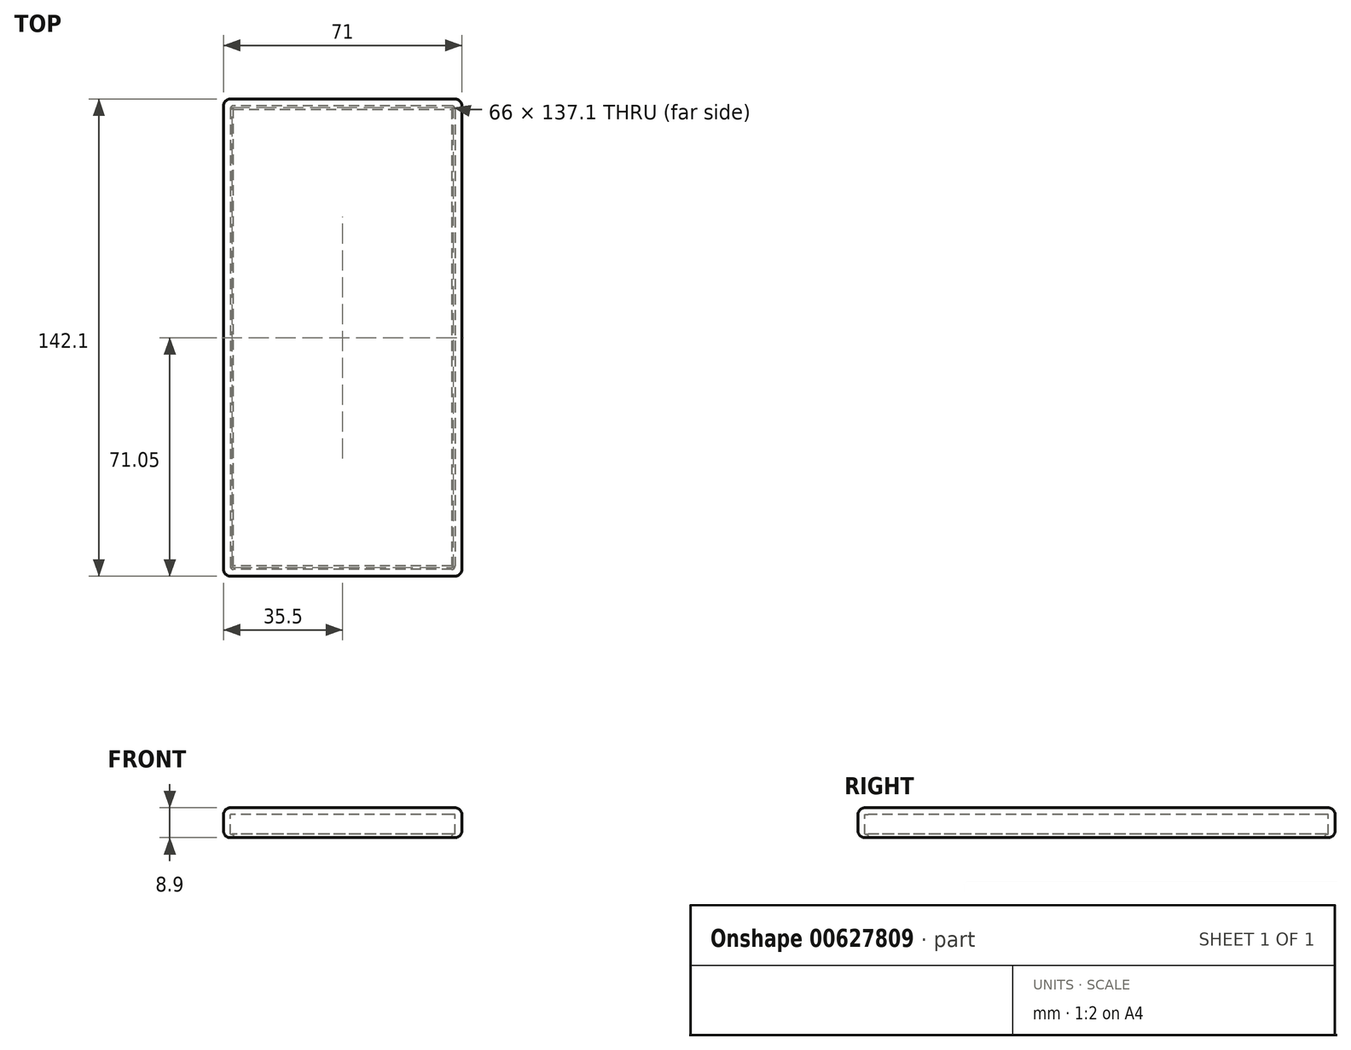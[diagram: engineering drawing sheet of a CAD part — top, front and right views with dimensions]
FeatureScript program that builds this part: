
annotation { "Feature Type Name" : "Feature", "Feature Type Description" : "" }
export const myFeature = defineFeature(function(context is Context, id is Id, definition is map)
    precondition{}
    {
        {
            assignVariable(context, id + "F0", {"name" : "iphone_thickness", "anyValue" : 6.9 * mm});
        }
        {
            assignVariable(context, id + "F1", {"name" : "case_thickness", "anyValue" : 2 * mm});
        }
        {
            var Q0;
            Q0=qCreatedBy(makeId("Top.planeOp"),FACE);
            var sketch = newSketch(context, id + "F2", { "sketchPlane" : qUnion([Q0])});
            skLineSegment(sketch, "E0.bottom", {"start": v(33.5, 69.05) * mm, "end": v(-33.5, 69.05) * mm});
            skLineSegment(sketch, "E0.top", {"start": v(33.5, -69.05) * mm, "end": v(-33.5, -69.05) * mm});
            skLineSegment(sketch, "E0.left", {"start": v(33.5, 69.05) * mm, "end": v(33.5, -69.05) * mm});
            skLineSegment(sketch, "E0.right", {"start": v(-33.5, 69.05) * mm, "end": v(-33.5, -69.05) * mm});
            skPoint(sketch, "E0.middle", {"position": v(0, 0) * mm});
            skLineSegment(sketch, "E1.0", {"start": v(35.5, 71.05) * mm, "end": v(35.5, -71.05) * mm});
            skLineSegment(sketch, "E1.1", {"start": v(35.5, 71.05) * mm, "end": v(-35.5, 71.05) * mm});
            skLineSegment(sketch, "E1.2", {"start": v(-35.5, 71.05) * mm, "end": v(-35.5, -71.05) * mm});
            skLineSegment(sketch, "E1.3", {"start": v(35.5, -71.05) * mm, "end": v(-35.5, -71.05) * mm});
            skSolve(sketch);
        }
        {
            var Q0;
            Q0=makeQuery(id+"F2.imprint","IMPRINT",FACE,{"disambiguationData":[TD([[makeQuery(id+"F2.imprint","IMPRINT",EDGE,{"derivedFrom":sQuery(id+"F2.wireOp",EDGE,"E0.bottom")}),1.0]])]});
            var Q1;
            Q1=makeQuery(id+"F2.imprint","IMPRINT",FACE,{"disambiguationData":[TD([[makeQuery(id+"F2.imprint","IMPRINT",EDGE,{"derivedFrom":sQuery(id+"F2.wireOp",EDGE,"E0.bottom")}),-1.0]])]});
            extrude(context, id + "F3", {"entities" : qUnion([Q0, Q1]), "depth" : getVariable(context, 'case_thickness'), "offsetDistance" : 25 * mm});
        }
        {
            var Q0;
            Q0=makeQuery(id+"F2.imprint","IMPRINT",FACE,{"disambiguationData":[TD([[makeQuery(id+"F2.imprint","IMPRINT",EDGE,{"derivedFrom":sQuery(id+"F2.wireOp",EDGE,"E0.bottom")}),-1.0]])]});
            extrude(context, id + "F4", {"entities" : qUnion([Q0]), "operationType" : NewBodyOperationType.ADD, "oppositeDirection" : true, "depth" : getVariable(context, 'iphone_thickness'), "offsetDistance" : 25 * mm});
        }
        {
            var Q0;
            Q0=makeQuery(id+"F4.opExtrude","CAP_FACE",FACE,{"disambiguationData":[OSD([sQuery(id+"F2.wireOp",EDGE,"E0.bottom"),sQuery(id+"F2.wireOp",EDGE,"E0.top"),sQuery(id+"F2.wireOp",EDGE,"E0.left"),sQuery(id+"F2.wireOp",EDGE,"E0.right"),sQuery(id+"F2.wireOp",EDGE,"E1.0"),sQuery(id+"F2.wireOp",EDGE,"E1.1"),sQuery(id+"F2.wireOp",EDGE,"E1.2"),sQuery(id+"F2.wireOp",EDGE,"E1.3")])],"isStart":false});
            var sketch = newSketch(context, id + "F5", { "sketchPlane" : qUnion([Q0])});
            skLineSegment(sketch, "E2.0", {"start": v(33.5, 69.05) * mm, "end": v(-33.5, 69.05) * mm});
            skLineSegment(sketch, "E2.1", {"start": v(33.5, -69.05) * mm, "end": v(33.5, 69.05) * mm});
            skLineSegment(sketch, "E2.2", {"start": v(-33.5, -69.05) * mm, "end": v(-33.5, 69.05) * mm});
            skLineSegment(sketch, "E2.3", {"start": v(33.5, -69.05) * mm, "end": v(-33.5, -69.05) * mm});
            skLineSegment(sketch, "E3.0", {"start": v(32.5, 68.05) * mm, "end": v(-32.5, 68.05) * mm});
            skLineSegment(sketch, "E3.1", {"start": v(32.5, -68.05) * mm, "end": v(32.5, 68.05) * mm});
            skLineSegment(sketch, "E3.2", {"start": v(32.5, -68.05) * mm, "end": v(-32.5, -68.05) * mm});
            skLineSegment(sketch, "E3.3", {"start": v(-32.5, -68.05) * mm, "end": v(-32.5, 68.05) * mm});
            skLineSegment(sketch, "E4.0", {"start": v(-38.5, 74.05) * mm, "end": v(38.5, 74.05) * mm});
            skLineSegment(sketch, "E4.1", {"start": v(-38.5, -74.05) * mm, "end": v(-38.5, 74.05) * mm});
            skLineSegment(sketch, "E4.2", {"start": v(38.5, -74.05) * mm, "end": v(-38.5, -74.05) * mm});
            skLineSegment(sketch, "E4.3", {"start": v(38.5, 74.05) * mm, "end": v(38.5, -74.05) * mm});
            skSolve(sketch);
        }
        {
            var Q0;
            Q0=makeQuery(id+"F5.imprint","IMPRINT",FACE,{"disambiguationData":[TD([[makeQuery(id+"F5.imprint","IMPRINT",EDGE,{"derivedFrom":sQuery(id+"F5.wireOp",EDGE,"E2.0")}),1.0]])]});
            extrude(context, id + "F6", {"entities" : qUnion([Q0]), "operationType" : NewBodyOperationType.ADD, "oppositeDirection" : true, "depth" : 1 * mm, "offsetDistance" : 25 * mm});
        }
        {
            var Q0;
            Q0=makeQuery(id+"F4.opExtrude","CAP_EDGE",EDGE,{"disambiguationData":[OSD([sQuery(id+"F2.wireOp",EDGE,"E0.left")])],"isStart":true});
            var Q1;
            Q1=makeQuery(id+"F4.opExtrude","CAP_EDGE",EDGE,{"disambiguationData":[OSD([sQuery(id+"F2.wireOp",EDGE,"E1.2")])],"isStart":false});
            var Q2;
            Q2=makeQuery(id+"F3.opExtrude","CAP_EDGE",EDGE,{"disambiguationData":[OSD([sQuery(id+"F2.wireOp",EDGE,"E1.2")])],"isStart":false});
            var Q3;
            Q3=makeQuery(id+"F3.opExtrude","CAP_EDGE",EDGE,{"disambiguationData":[OSD([sQuery(id+"F2.wireOp",EDGE,"E1.1")])],"isStart":false});
            var Q4;
            Q4=makeQuery(id+"F3.opExtrude","CAP_EDGE",EDGE,{"disambiguationData":[OSD([sQuery(id+"F2.wireOp",EDGE,"E1.0")])],"isStart":false});
            var Q5;
            Q5=makeQuery(id+"F3.opExtrude","CAP_EDGE",EDGE,{"disambiguationData":[OSD([sQuery(id+"F2.wireOp",EDGE,"E1.3")])],"isStart":false});
            var Q6;
            {var subQ0=sQuery(id+"F2.wireOp",EDGE,"E1.3");var subQ1=sQuery(id+"F2.wireOp",EDGE,"E1.2");Q6=makeQuery(id+"F4.boolean.opBoolean","MERGE",EDGE,{"derivedFrom":[makeQuery(id+"F3.opExtrude","SWEPT_EDGE",EDGE,{"disambiguationData":[OSD([subQ1,subQ0])]}),makeQuery(id+"F4.opExtrude","SWEPT_EDGE",EDGE,{"disambiguationData":[OSD([subQ1,subQ0])]})]});}
            var Q7;
            {var subQ0=sQuery(id+"F2.wireOp",EDGE,"E1.3");var subQ1=sQuery(id+"F2.wireOp",EDGE,"E1.0");Q7=makeQuery(id+"F4.boolean.opBoolean","MERGE",EDGE,{"derivedFrom":[makeQuery(id+"F3.opExtrude","SWEPT_EDGE",EDGE,{"disambiguationData":[OSD([subQ1,subQ0])]}),makeQuery(id+"F4.opExtrude","SWEPT_EDGE",EDGE,{"disambiguationData":[OSD([subQ1,subQ0])]})]});}
            var Q8;
            {var subQ0=sQuery(id+"F2.wireOp",EDGE,"E1.1");var subQ1=sQuery(id+"F2.wireOp",EDGE,"E1.0");Q8=makeQuery(id+"F4.boolean.opBoolean","MERGE",EDGE,{"derivedFrom":[makeQuery(id+"F3.opExtrude","SWEPT_EDGE",EDGE,{"disambiguationData":[OSD([subQ1,subQ0])]}),makeQuery(id+"F4.opExtrude","SWEPT_EDGE",EDGE,{"disambiguationData":[OSD([subQ1,subQ0])]})]});}
            var Q9;
            {var subQ0=sQuery(id+"F2.wireOp",EDGE,"E1.2");var subQ1=sQuery(id+"F2.wireOp",EDGE,"E1.1");Q9=makeQuery(id+"F4.boolean.opBoolean","MERGE",EDGE,{"derivedFrom":[makeQuery(id+"F3.opExtrude","SWEPT_EDGE",EDGE,{"disambiguationData":[OSD([subQ1,subQ0])]}),makeQuery(id+"F4.opExtrude","SWEPT_EDGE",EDGE,{"disambiguationData":[OSD([subQ1,subQ0])]})]});}
            var Q10;
            Q10=makeQuery(id+"F4.opExtrude","CAP_EDGE",EDGE,{"disambiguationData":[OSD([sQuery(id+"F2.wireOp",EDGE,"E1.1")])],"isStart":false});
            var Q11;
            Q11=makeQuery(id+"F4.opExtrude","CAP_EDGE",EDGE,{"disambiguationData":[OSD([sQuery(id+"F2.wireOp",EDGE,"E1.0")])],"isStart":false});
            var Q12;
            Q12=makeQuery(id+"F4.opExtrude","CAP_EDGE",EDGE,{"disambiguationData":[OSD([sQuery(id+"F2.wireOp",EDGE,"E1.3")])],"isStart":false});
            var Q13;
            Q13=makeQuery(id+"F4.opExtrude","CAP_EDGE",EDGE,{"disambiguationData":[OSD([sQuery(id+"F2.wireOp",EDGE,"E0.top")])],"isStart":true});
            var Q14;
            Q14=makeQuery(id+"F4.opExtrude","CAP_EDGE",EDGE,{"disambiguationData":[OSD([sQuery(id+"F2.wireOp",EDGE,"E0.right")])],"isStart":true});
            var Q15;
            Q15=makeQuery(id+"F4.opExtrude","CAP_EDGE",EDGE,{"disambiguationData":[OSD([sQuery(id+"F2.wireOp",EDGE,"E0.bottom")])],"isStart":true});
            fillet(context, id + "F7", {"entities" : qUnion([Q0, Q1, Q2, Q3, Q4, Q5, Q6, Q7, Q8, Q9, Q10, Q11, Q12, Q13, Q14, Q15]), "radius" : 2 * mm, "tangentPropagation" : true, "allowEdgeOverflow" : false});
        }
        {
            var Q0;
            Q0=makeQuery(id+"F6.opExtrude","CAP_EDGE",EDGE,{"disambiguationData":[OSD([sQuery(id+"F5.wireOp",EDGE,"E3.3")])],"isStart":false});
            var Q1;
            Q1=makeQuery(id+"F6.opExtrude","CAP_EDGE",EDGE,{"disambiguationData":[OSD([sQuery(id+"F5.wireOp",EDGE,"E3.0")])],"isStart":false});
            var Q2;
            Q2=makeQuery(id+"F6.opExtrude","CAP_EDGE",EDGE,{"disambiguationData":[OSD([sQuery(id+"F5.wireOp",EDGE,"E3.1")])],"isStart":false});
            var Q3;
            Q3=makeQuery(id+"F6.opExtrude","CAP_EDGE",EDGE,{"disambiguationData":[OSD([sQuery(id+"F5.wireOp",EDGE,"E3.2")])],"isStart":false});
            var Q4;
            Q4=makeQuery(id+"F6.opExtrude","CAP_EDGE",EDGE,{"disambiguationData":[OSD([sQuery(id+"F5.wireOp",EDGE,"E3.1")])],"isStart":true});
            var Q5;
            Q5=makeQuery(id+"F6.opExtrude","CAP_EDGE",EDGE,{"disambiguationData":[OSD([sQuery(id+"F5.wireOp",EDGE,"E3.2")])],"isStart":true});
            var Q6;
            Q6=makeQuery(id+"F6.opExtrude","CAP_EDGE",EDGE,{"disambiguationData":[OSD([sQuery(id+"F5.wireOp",EDGE,"E3.0")])],"isStart":true});
            var Q7;
            Q7=makeQuery(id+"F7.opFillet","BLEND_EDGE",EDGE,{"blendedFrom":[makeQuery(id+"F4.opExtrude","CAP_EDGE",EDGE,{"disambiguationData":[OSD([sQuery(id+"F2.wireOp",EDGE,"E0.left")])],"isStart":true}),makeQuery(id+"F3.opExtrude","CAP_FACE",FACE,{"disambiguationData":[OSD([sQuery(id+"F2.wireOp",EDGE,"E1.0"),sQuery(id+"F2.wireOp",EDGE,"E1.1"),sQuery(id+"F2.wireOp",EDGE,"E1.2"),sQuery(id+"F2.wireOp",EDGE,"E1.3")])],"isStart":true})],"blendedInto":[makeQuery(id+"F3.opExtrude","CAP_FACE",FACE,{"disambiguationData":[OSD([sQuery(id+"F2.wireOp",EDGE,"E1.0"),sQuery(id+"F2.wireOp",EDGE,"E1.1"),sQuery(id+"F2.wireOp",EDGE,"E1.2"),sQuery(id+"F2.wireOp",EDGE,"E1.3")])],"isStart":true})]});
            var Q8;
            Q8=makeQuery(id+"F6.opExtrude","CAP_EDGE",EDGE,{"disambiguationData":[OSD([sQuery(id+"F5.wireOp",EDGE,"E3.3")])],"isStart":true});
            fillet(context, id + "F8", {"entities" : qUnion([Q0, Q1, Q2, Q3, Q4, Q5, Q6, Q7, Q8]), "radius" : 0.5 * mm, "tangentPropagation" : true, "allowEdgeOverflow" : false});
        }
        {
            var Q0;
            Q0=makeQuery(id+"F4.opExtrude","SWEPT_EDGE",EDGE,{"disambiguationData":[OSD([sQuery(id+"F2.wireOp",EDGE,"E0.top"),sQuery(id+"F2.wireOp",EDGE,"E0.right")])]});
            var Q1;
            Q1=makeQuery(id+"F4.opExtrude","SWEPT_EDGE",EDGE,{"disambiguationData":[OSD([sQuery(id+"F2.wireOp",EDGE,"E0.top"),sQuery(id+"F2.wireOp",EDGE,"E0.left")])]});
            var Q2;
            Q2=makeQuery(id+"F4.opExtrude","SWEPT_EDGE",EDGE,{"disambiguationData":[OSD([sQuery(id+"F2.wireOp",EDGE,"E0.bottom"),sQuery(id+"F2.wireOp",EDGE,"E0.left")])]});
            var Q3;
            Q3=makeQuery(id+"F4.opExtrude","SWEPT_EDGE",EDGE,{"disambiguationData":[OSD([sQuery(id+"F2.wireOp",EDGE,"E0.bottom"),sQuery(id+"F2.wireOp",EDGE,"E0.right")])]});
            var Q4;
            Q4=makeQuery(id+"F8.opFillet","BLEND_EDGE",EDGE,{"blendedFrom":[makeQuery(id+"F6.opExtrude","CAP_EDGE",EDGE,{"disambiguationData":[OSD([sQuery(id+"F5.wireOp",EDGE,"E3.2")])],"isStart":false}),makeQuery(id+"F6.opExtrude","CAP_EDGE",EDGE,{"disambiguationData":[OSD([sQuery(id+"F5.wireOp",EDGE,"E3.3")])],"isStart":false})],"blendedInto":[]});
            var Q5;
            Q5=makeQuery(id+"F8.opFillet","BLEND_EDGE",EDGE,{"blendedFrom":[makeQuery(id+"F6.opExtrude","CAP_EDGE",EDGE,{"disambiguationData":[OSD([sQuery(id+"F5.wireOp",EDGE,"E3.1")])],"isStart":false}),makeQuery(id+"F6.opExtrude","CAP_EDGE",EDGE,{"disambiguationData":[OSD([sQuery(id+"F5.wireOp",EDGE,"E3.2")])],"isStart":false})],"blendedInto":[]});
            var Q6;
            {var subQ0=sQuery(id+"F2.wireOp",EDGE,"E0.top");Q6=makeQuery(id+"F7.opFillet","BLEND_EDGE",EDGE,{"blendedFrom":[makeQuery(id+"F4.opExtrude","CAP_EDGE",EDGE,{"disambiguationData":[OSD([subQ0])],"isStart":true}),makeQuery(id+"F4.opExtrude","SWEPT_FACE",FACE,{"disambiguationData":[OSD([subQ0])]})],"blendedInto":[makeQuery(id+"F4.opExtrude","SWEPT_FACE",FACE,{"disambiguationData":[OSD([subQ0])]})]});}
            var Q7;
            Q7=makeQuery(id+"F8.opFillet","BLEND_EDGE",EDGE,{"blendedFrom":[makeQuery(id+"F6.opExtrude","CAP_EDGE",EDGE,{"disambiguationData":[OSD([sQuery(id+"F5.wireOp",EDGE,"E3.0")])],"isStart":false}),makeQuery(id+"F6.opExtrude","CAP_EDGE",EDGE,{"disambiguationData":[OSD([sQuery(id+"F5.wireOp",EDGE,"E3.1")])],"isStart":false})],"blendedInto":[]});
            var Q8;
            Q8=makeQuery(id+"F8.opFillet","BLEND_EDGE",EDGE,{"blendedFrom":[makeQuery(id+"F6.opExtrude","CAP_EDGE",EDGE,{"disambiguationData":[OSD([sQuery(id+"F5.wireOp",EDGE,"E3.0")])],"isStart":false}),makeQuery(id+"F6.opExtrude","CAP_EDGE",EDGE,{"disambiguationData":[OSD([sQuery(id+"F5.wireOp",EDGE,"E3.3")])],"isStart":false})],"blendedInto":[]});
            fillet(context, id + "F9", {"entities" : qUnion([Q0, Q1, Q2, Q3, Q4, Q5, Q6, Q7, Q8]), "radius" : 1 * mm, "tangentPropagation" : true, "allowEdgeOverflow" : false});
        }
    });
